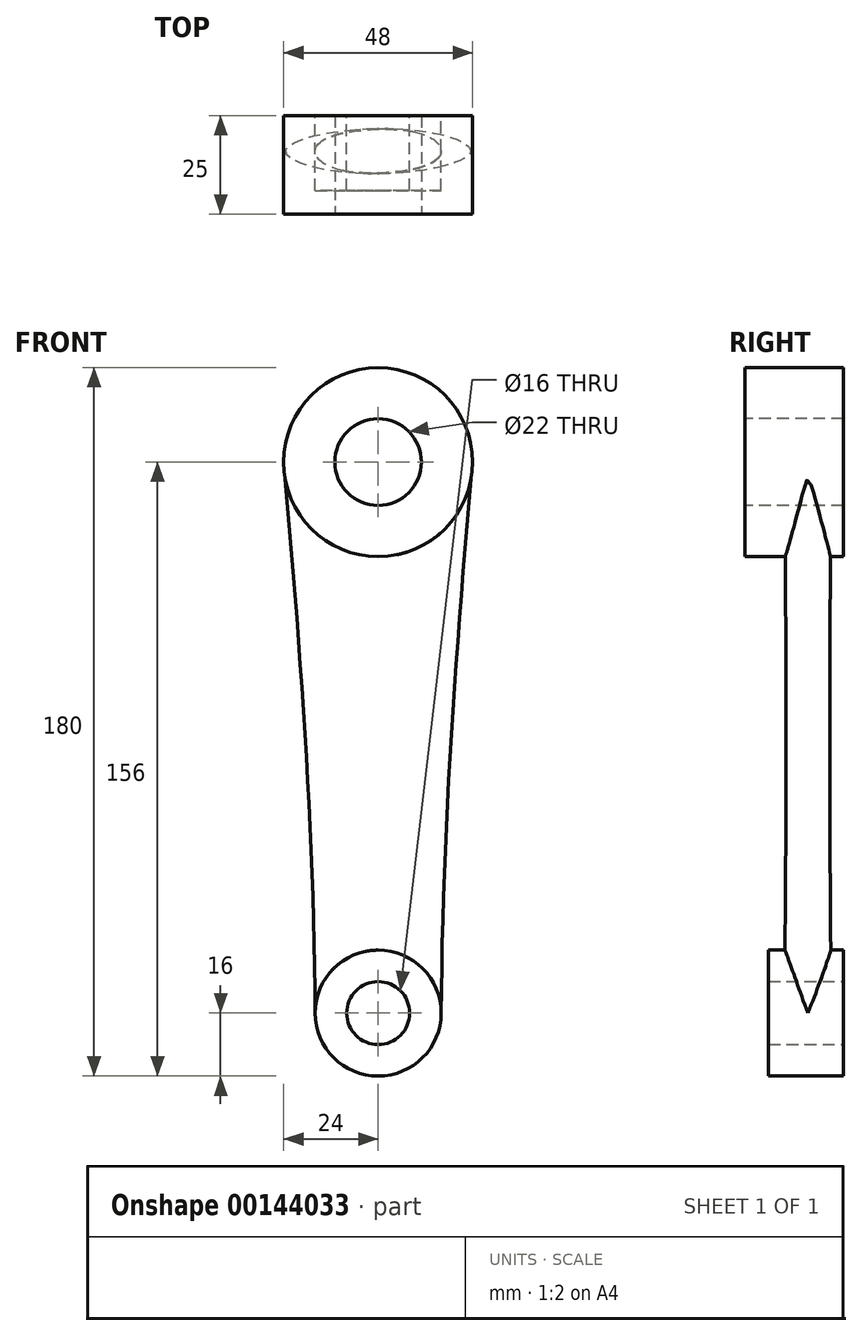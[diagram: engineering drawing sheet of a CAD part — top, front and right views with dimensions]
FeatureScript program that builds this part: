
annotation { "Feature Type Name" : "Feature", "Feature Type Description" : "" }
export const myFeature = defineFeature(function(context is Context, id is Id, definition is map)
    precondition{}
    {
        {
            var Q0;
            Q0=qCreatedBy(makeId("Front.planeOp"),FACE);
            var sketch = newSketch(context, id + "F0", { "sketchPlane" : qUnion([Q0])});
            skCircle(sketch, "E0", {"center": v(0, 0) * mm, "radius": 8 * mm});
            skCircle(sketch, "E1", {"center": v(0, 0) * mm, "radius": 16 * mm});
            skSolve(sketch);
        }
        {
            var Q0;
            Q0 = qSketchRegion(id + "F0", true);
            extrude(context, id + "F1", {"entities" : qUnion([Q0]), "endBound" : BoundingType.SYMMETRIC, "depth" : 19 * mm});
        }
        {
            var Q0;
            Q0=qCreatedBy(makeId("Front.planeOp"),FACE);
            var sketch = newSketch(context, id + "F2", { "sketchPlane" : qUnion([Q0])});
            skCircle(sketch, "E2", {"center": v(0, 140) * mm, "radius": 11 * mm});
            skCircle(sketch, "E3", {"center": v(0, 140) * mm, "radius": 24 * mm});
            skSolve(sketch);
        }
        {
            var Q0;
            Q0 = qSketchRegion(id + "F2", true);
            extrude(context, id + "F3", {"entities" : qUnion([Q0]), "oppositeDirection" : true, "depth" : 9.5 * mm});
        }
        {
            var Q0;
            Q0=makeQuery(id+"F3.opExtrude","CAP_FACE",FACE,{"disambiguationData":[OSD([sQuery(id+"F2.wireOp",EDGE,"E2"),sQuery(id+"F2.wireOp",EDGE,"E3")])],"isStart":true});
            var sketch = newSketch(context, id + "F4", { "sketchPlane" : qUnion([Q0])});
            skCircle(sketch, "E4.0", {"center": v(0, 140) * mm, "radius": 24 * mm});
            skCircle(sketch, "E5.0", {"center": v(0, 140) * mm, "radius": 11 * mm});
            skSolve(sketch);
        }
        {
            var Q0;
            Q0 = qSketchRegion(id + "F4", true);
            extrude(context, id + "F5", {"entities" : qUnion([Q0]), "operationType" : NewBodyOperationType.ADD, "depth" : (25 - 9.5) * mm});
        }
        {
            var Q0;
            Q0=qCreatedBy(makeId("Top.planeOp"),FACE);
            var sketch = newSketch(context, id + "F6", { "sketchPlane" : qUnion([Q0])});
            skEllipse(sketch, "E6", {"center": v(0, 0.5) * mm, "majorRadius": 16 * mm, "minorRadius": 6 * mm, "majorAxis": v(1, 0)});
            skPoint(sketch, "E7", {"position": v(0, 6.5) * mm});
            skLineSegment(sketch, "E8", {"start": v(16, 9.5) * mm, "end": v(16, -9.5) * mm, "construction": true});
            skSolve(sketch);
        }
        {
            var Q0;
            Q0=sQuery(id+"F2.wireOp",VERTEX,"E2.center");
            var Q1;
            Q1=qCreatedBy(makeId("Top.planeOp"),FACE);
            cPlane(context, id + "F7", {"entities" : qUnion([Q0, Q1]), "cplaneType" : CPlaneType.PLANE_POINT, "offset" : 25 * mm, "width" : 150 * mm, "height" : 150 * mm});
        }
        {
            var Q0;
            Q0=qCreatedBy(id+"F7.planeOp",FACE);
            var sketch = newSketch(context, id + "F8", { "sketchPlane" : qUnion([Q0])});
            skEllipse(sketch, "E9", {"center": v(0, 0.5) * mm, "majorRadius": 24 * mm, "minorRadius": 6 * mm, "majorAxis": v(1, 0)});
            skPoint(sketch, "E10", {"position": v(0, 6.5) * mm});
            skLineSegment(sketch, "E11", {"start": v(24, 9.5) * mm, "end": v(24, -15.5) * mm, "construction": true});
            skSolve(sketch);
        }
        {
            var Q0;
            Q0=makeQuery(id+"F6.imprint","IMPRINT",FACE,{"disambiguationData":[TD([[makeQuery(id+"F6.imprint","IMPRINT",EDGE,{"derivedFrom":sQuery(id+"F6.wireOp",EDGE,"E6")}),1.0]])]});
            var Q1;
            Q1=makeQuery(id+"F8.imprint","IMPRINT",FACE,{"disambiguationData":[TD([[makeQuery(id+"F8.imprint","IMPRINT",EDGE,{"derivedFrom":sQuery(id+"F8.wireOp",EDGE,"E9")}),1.0]])]});
            loft(context, id + "F9", {"operationType" : NewBodyOperationType.ADD, "sheetProfilesArray" : [{ "sheetProfileEntities" : qUnion([Q0]) }, { "sheetProfileEntities" : qUnion([Q1]) }]});
        }
        {
            var Q0;
            Q0=makeQuery(id+"F1.opExtrude","CAP_FACE",FACE,{"disambiguationData":[OSD([sQuery(id+"F0.wireOp",EDGE,"E0"),sQuery(id+"F0.wireOp",EDGE,"E1")])],"isStart":false});
            var sketch = newSketch(context, id + "F10", { "sketchPlane" : qUnion([Q0])});
            skCircle(sketch, "E12.0", {"center": v(0, 0) * mm, "radius": 8 * mm});
            skSolve(sketch);
        }
        {
            var Q0;
            Q0 = qSketchRegion(id + "F10", true);
            extrude(context, id + "F11", {"entities" : qUnion([Q0]), "operationType" : NewBodyOperationType.REMOVE, "endBound" : BoundingType.THROUGH_ALL, "oppositeDirection" : true, "depth" : 25 * mm});
        }
        {
            var Q0;
            Q0=makeQuery(id+"F5.opExtrude","CAP_FACE",FACE,{"disambiguationData":[OSD([sQuery(id+"F4.wireOp",EDGE,"E4.0"),sQuery(id+"F4.wireOp",EDGE,"E5.0")])],"isStart":false});
            var sketch = newSketch(context, id + "F12", { "sketchPlane" : qUnion([Q0])});
            skCircle(sketch, "E13.0", {"center": v(0, 140) * mm, "radius": 11 * mm});
            skSolve(sketch);
        }
        {
            var Q0;
            Q0 = qSketchRegion(id + "F12", true);
            extrude(context, id + "F13", {"entities" : qUnion([Q0]), "operationType" : NewBodyOperationType.REMOVE, "endBound" : BoundingType.THROUGH_ALL, "oppositeDirection" : true, "depth" : 25 * mm});
        }
    });
